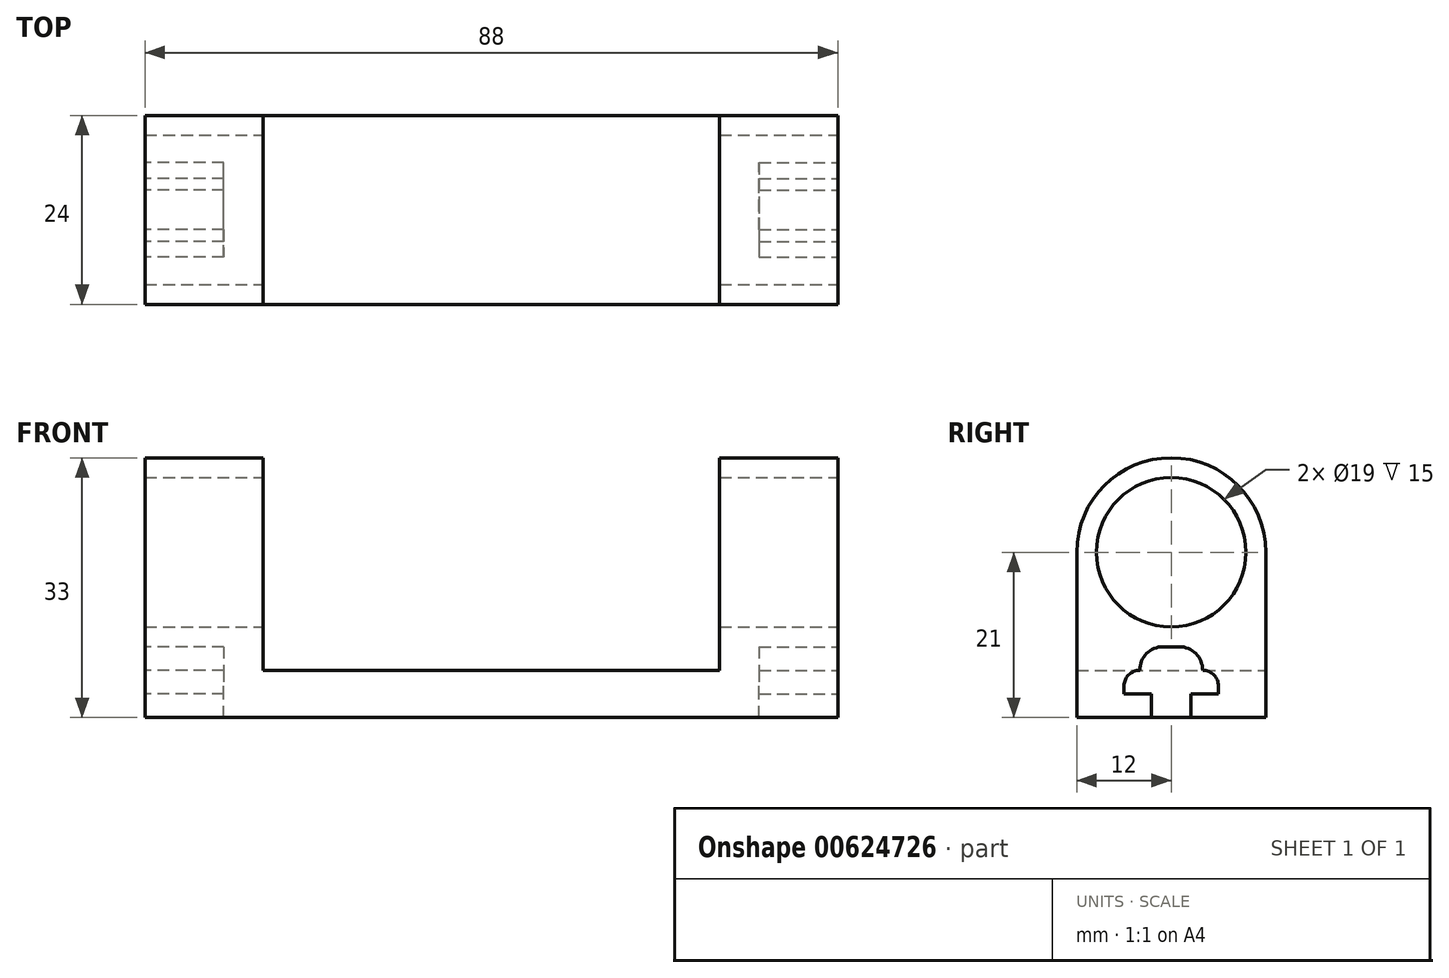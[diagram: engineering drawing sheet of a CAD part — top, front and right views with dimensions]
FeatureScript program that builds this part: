
annotation { "Feature Type Name" : "Feature", "Feature Type Description" : "" }
export const myFeature = defineFeature(function(context is Context, id is Id, definition is map)
    precondition{}
    {
        {
            var Q0;
            Q0=qCreatedBy(makeId("Right.planeOp"),FACE);
            var sketch = newSketch(context, id + "F0", { "sketchPlane" : qUnion([Q0])});
            skLineSegment(sketch, "E0.bottom", {"start": v(-12, 33) * mm, "end": v(12, 33) * mm});
            skLineSegment(sketch, "E0.top", {"start": v(-12, 0) * mm, "end": v(12, 0) * mm});
            skLineSegment(sketch, "E0.left", {"start": v(-12, 33) * mm, "end": v(-12, 0) * mm});
            skLineSegment(sketch, "E0.right", {"start": v(12, 33) * mm, "end": v(12, 0) * mm});
            skCircle(sketch, "E1", {"center": v(0, 21) * mm, "radius": 9.5 * mm});
            skLineSegment(sketch, "E2", {"start": v(-15.84, 21) * mm, "end": v(23, 21) * mm, "construction": true});
            skLineSegment(sketch, "E3", {"start": v(0, 55.63) * mm, "end": v(0, -4.9) * mm, "construction": true});
            skCircle(sketch, "E4.0", {"center": v(0, 21) * mm, "radius": 12 * mm});
            skLineSegment(sketch, "E5", {"start": v(2.5, 0) * mm, "end": v(2.5, 3) * mm});
            skLineSegment(sketch, "E6", {"start": v(2.5, 3) * mm, "end": v(6, 3) * mm});
            skLineSegment(sketch, "E7", {"start": v(6, 3) * mm, "end": v(6, 6) * mm});
            skLineSegment(sketch, "E8", {"start": v(6, 6) * mm, "end": v(4, 6) * mm});
            skLineSegment(sketch, "E9", {"start": v(4, 6) * mm, "end": v(4, 9) * mm});
            skLineSegment(sketch, "E10", {"start": v(4, 9) * mm, "end": v(0, 9) * mm});
            skLineSegment(sketch, "E11.MirrorCS", {"start": v(-4, 9) * mm, "end": v(0, 9) * mm});
            skLineSegment(sketch, "E12.MirrorCS", {"start": v(-4, 6) * mm, "end": v(-4, 9) * mm});
            skLineSegment(sketch, "E13.MirrorCS", {"start": v(-6, 6) * mm, "end": v(-4, 6) * mm});
            skLineSegment(sketch, "E14.MirrorCS", {"start": v(-6, 3) * mm, "end": v(-6, 6) * mm});
            skLineSegment(sketch, "E15.MirrorCS", {"start": v(-2.5, 3) * mm, "end": v(-6, 3) * mm});
            skLineSegment(sketch, "E16.MirrorCS", {"start": v(-2.5, 0) * mm, "end": v(-2.5, 3) * mm});
            skSolve(sketch);
        }
        {
            var Q0;
            {var subQ0=sQuery(id+"F0.wireOp",EDGE,"E0.top");Q0=makeQuery(id+"F0.imprint","IMPRINT",FACE,{"disambiguationData":[TD([[makeQuery(id+"F0.imprint","IMPRINT",EDGE,{"derivedFrom":subQ0}),1.0]])]});}
            var Q1;
            Q1=makeQuery(id+"F0.imprint","IMPRINT",FACE,{"disambiguationData":[TD([[makeQuery(id+"F0.imprint","IMPRINT",EDGE,{"derivedFrom":sQuery(id+"F0.wireOp",EDGE,"E1")}),-1.0]])]});
            var Q2;
            {var subQ7=sQuery(id+"F0.wireOp",EDGE,"E5");Q2=makeQuery(id+"F0.imprint","IMPRINT",FACE,{"disambiguationData":[TD([[makeQuery(id+"F0.imprint","IMPRINT",EDGE,{"derivedFrom":subQ7}),1.0]])]});}
            var Q3;
            {var subQ1=sQuery(id+"F0.wireOp",EDGE,"E10");Q3=makeQuery(id+"F0.imprint","IMPRINT",FACE,{"disambiguationData":[TD([[makeQuery(id+"F0.imprint","IMPRINT",EDGE,{"derivedFrom":subQ1}),1.0]])]});}
            extrude(context, id + "F1", {"entities" : qUnion([Q0, Q1, Q2, Q3]), "oppositeDirection" : true, "depth" : 88 * mm, "offsetDistance" : 25 * mm});
        }
        {
            var Q0;
            Q0=qCreatedBy(makeId("Front.planeOp"),FACE);
            var sketch = newSketch(context, id + "F2", { "sketchPlane" : qUnion([Q0])});
            skLineSegment(sketch, "E17", {"start": v(-15, 43.82) * mm, "end": v(-15, -4.27) * mm, "construction": true});
            skLineSegment(sketch, "E18", {"start": v(-73, 48.33) * mm, "end": v(-73, -7.38) * mm, "construction": true});
            skLineSegment(sketch, "E19", {"start": v(-97.26, 6) * mm, "end": v(5.38, 6) * mm, "construction": true});
            skLineSegment(sketch, "E20.bottom", {"start": v(-73, 33) * mm, "end": v(-15, 33) * mm});
            skLineSegment(sketch, "E20.top", {"start": v(-73, 6) * mm, "end": v(-15, 6) * mm});
            skLineSegment(sketch, "E20.left", {"start": v(-73, 33) * mm, "end": v(-73, 6) * mm});
            skLineSegment(sketch, "E20.right", {"start": v(-15, 33) * mm, "end": v(-15, 6) * mm});
            skLineSegment(sketch, "E21", {"start": v(-96.84, 33) * mm, "end": v(8.35, 33) * mm, "construction": true});
            skSolve(sketch);
        }
        {
            var Q0;
            Q0=makeQuery(id+"F2.imprint","IMPRINT",FACE,{"disambiguationData":[TD([[makeQuery(id+"F2.imprint","IMPRINT",EDGE,{"derivedFrom":sQuery(id+"F2.wireOp",EDGE,"E20.bottom")}),-1.0]])]});
            extrude(context, id + "F3", {"entities" : qUnion([Q0]), "operationType" : NewBodyOperationType.REMOVE, "endBound" : BoundingType.SYMMETRIC, "depth" : 25 * mm, "offsetDistance" : 25 * mm});
        }
        {
            var Q0;
            {var subQ7=sQuery(id+"F0.wireOp",EDGE,"E5");Q0=makeQuery(id+"F0.imprint","IMPRINT",FACE,{"disambiguationData":[TD([[makeQuery(id+"F0.imprint","IMPRINT",EDGE,{"derivedFrom":subQ7}),1.0]])]});}
            extrude(context, id + "F4", {"entities" : qUnion([Q0]), "operationType" : NewBodyOperationType.REMOVE, "oppositeDirection" : true, "depth" : 10 * mm, "offsetDistance" : 25 * mm});
        }
        {
            var Q0;
            Q0=makeQuery(id+"F1.opExtrude","CAP_FACE",FACE,{"disambiguationData":[OSD([sQuery(id+"F0.wireOp",EDGE,"E0.top"),sQuery(id+"F0.wireOp",EDGE,"E0.left"),sQuery(id+"F0.wireOp",EDGE,"E0.right"),sQuery(id+"F0.wireOp",EDGE,"E1"),sQuery(id+"F0.wireOp",EDGE,"E4.0")])],"isStart":false});
            var sketch = newSketch(context, id + "F5", { "sketchPlane" : qUnion([Q0])});
            skLineSegment(sketch, "E22.0", {"start": v(-2.5, 0) * mm, "end": v(-2.5, 3) * mm});
            skLineSegment(sketch, "E22.1", {"start": v(6, 6) * mm, "end": v(4, 6) * mm});
            skLineSegment(sketch, "E22.2", {"start": v(-4, 6) * mm, "end": v(-4, 9) * mm});
            skLineSegment(sketch, "E22.3", {"start": v(-6, 6) * mm, "end": v(-4, 6) * mm});
            skLineSegment(sketch, "E22.4", {"start": v(-6, 3) * mm, "end": v(-6, 6) * mm});
            skLineSegment(sketch, "E22.5", {"start": v(-2.5, 3) * mm, "end": v(-6, 3) * mm});
            skLineSegment(sketch, "E22.6", {"start": v(-4, 9) * mm, "end": v(0, 9) * mm});
            skLineSegment(sketch, "E22.7", {"start": v(4, 9) * mm, "end": v(0, 9) * mm});
            skLineSegment(sketch, "E22.8", {"start": v(6, 3) * mm, "end": v(6, 6) * mm});
            skLineSegment(sketch, "E22.9", {"start": v(4, 6) * mm, "end": v(4, 9) * mm});
            skLineSegment(sketch, "E22.10", {"start": v(2.5, 3) * mm, "end": v(6, 3) * mm});
            skLineSegment(sketch, "E22.11", {"start": v(2.5, 0) * mm, "end": v(2.5, 3) * mm});
            skCircle(sketch, "E23.0", {"center": v(0, 21) * mm, "radius": 12 * mm});
            skSolve(sketch);
        }
        {
            var Q0;
            {var subQ0=sQuery(id+"F5.wireOp",EDGE,"E22.0");Q0=makeQuery(id+"F5.imprint","IMPRINT",FACE,{"disambiguationData":[TD([[makeQuery(id+"F5.imprint","IMPRINT",EDGE,{"derivedFrom":subQ0}),-1.0]])]});}
            extrude(context, id + "F6", {"entities" : qUnion([Q0]), "operationType" : NewBodyOperationType.REMOVE, "oppositeDirection" : true, "depth" : 10 * mm, "offsetDistance" : 25 * mm});
        }
        {
            var Q0;
            Q0=makeQuery(id+"F6.boolean.opBoolean","COPY",EDGE,{"derivedFrom":makeQuery(id+"F6.opExtrude","SWEPT_EDGE",EDGE,{"disambiguationData":[OSD([sQuery(id+"F5.wireOp",EDGE,"E22.2"),sQuery(id+"F5.wireOp",EDGE,"E22.6")])]})});
            var Q1;
            Q1=makeQuery(id+"F6.boolean.opBoolean","COPY",EDGE,{"derivedFrom":makeQuery(id+"F6.opExtrude","SWEPT_EDGE",EDGE,{"disambiguationData":[OSD([sQuery(id+"F5.wireOp",EDGE,"E22.7"),sQuery(id+"F5.wireOp",EDGE,"E22.9")])]})});
            var Q2;
            Q2=makeQuery(id+"F4.boolean.opBoolean","COPY",EDGE,{"derivedFrom":makeQuery(id+"F4.opExtrude","SWEPT_EDGE",EDGE,{"disambiguationData":[OSD([sQuery(id+"F0.wireOp",EDGE,"E11.MirrorCS"),sQuery(id+"F0.wireOp",EDGE,"E12.MirrorCS")])]})});
            var Q3;
            Q3=makeQuery(id+"F4.boolean.opBoolean","COPY",EDGE,{"derivedFrom":makeQuery(id+"F4.opExtrude","SWEPT_EDGE",EDGE,{"disambiguationData":[OSD([sQuery(id+"F0.wireOp",EDGE,"E9"),sQuery(id+"F0.wireOp",EDGE,"E10")])]})});
            fillet(context, id + "F7", {"entities" : qUnion([Q0, Q1, Q2, Q3]), "radius" : 3 * mm, "tangentPropagation" : true, "allowEdgeOverflow" : false});
        }
        {
            var Q0;
            Q0=makeQuery(id+"F6.boolean.opBoolean","COPY",EDGE,{"derivedFrom":makeQuery(id+"F6.opExtrude","SWEPT_EDGE",EDGE,{"disambiguationData":[OSD([sQuery(id+"F5.wireOp",EDGE,"E22.1"),sQuery(id+"F5.wireOp",EDGE,"E22.8")])]})});
            var Q1;
            Q1=makeQuery(id+"F6.boolean.opBoolean","COPY",EDGE,{"derivedFrom":makeQuery(id+"F6.opExtrude","SWEPT_EDGE",EDGE,{"disambiguationData":[OSD([sQuery(id+"F5.wireOp",EDGE,"E22.3"),sQuery(id+"F5.wireOp",EDGE,"E22.4")])]})});
            var Q2;
            Q2=makeQuery(id+"F4.boolean.opBoolean","COPY",EDGE,{"derivedFrom":makeQuery(id+"F4.opExtrude","SWEPT_EDGE",EDGE,{"disambiguationData":[OSD([sQuery(id+"F0.wireOp",EDGE,"E7"),sQuery(id+"F0.wireOp",EDGE,"E8")])]})});
            var Q3;
            Q3=makeQuery(id+"F4.boolean.opBoolean","COPY",EDGE,{"derivedFrom":makeQuery(id+"F4.opExtrude","SWEPT_EDGE",EDGE,{"disambiguationData":[OSD([sQuery(id+"F0.wireOp",EDGE,"E13.MirrorCS"),sQuery(id+"F0.wireOp",EDGE,"E14.MirrorCS")])]})});
            fillet(context, id + "F8", {"entities" : qUnion([Q0, Q1, Q2, Q3]), "radius" : 2 * mm, "tangentPropagation" : true, "allowEdgeOverflow" : false});
        }
    });
